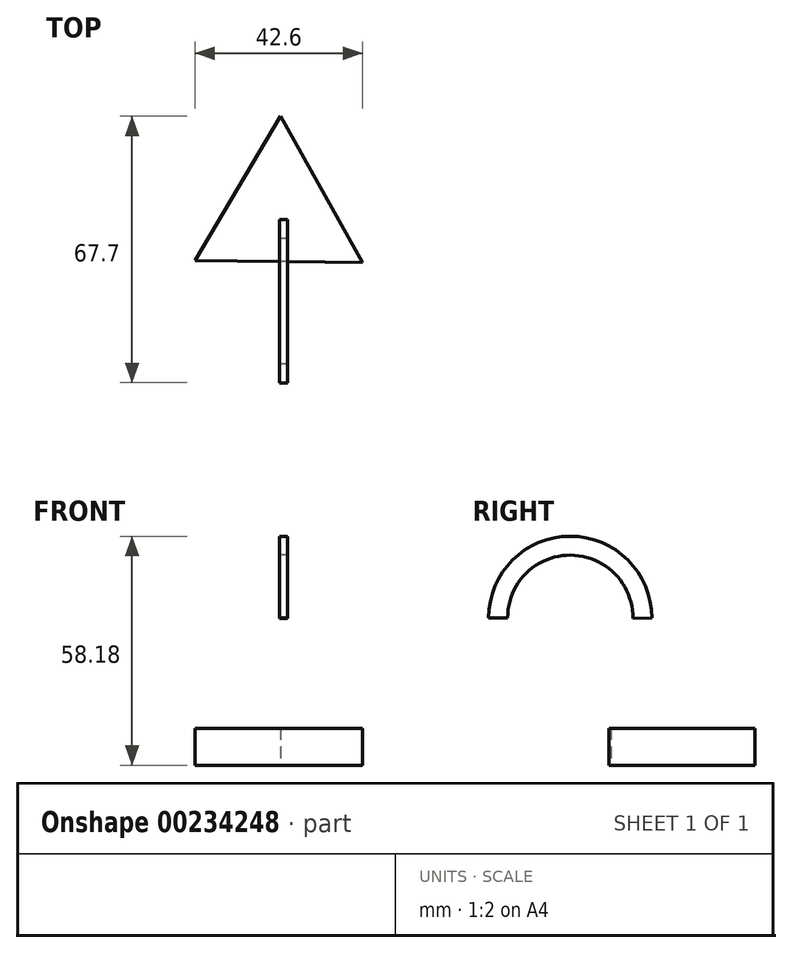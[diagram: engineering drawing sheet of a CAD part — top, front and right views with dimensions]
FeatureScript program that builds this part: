
annotation { "Feature Type Name" : "Feature", "Feature Type Description" : "" }
export const myFeature = defineFeature(function(context is Context, id is Id, definition is map)
    precondition{}
    {
        {
            var Q0;
            Q0=qCreatedBy(makeId("Top.planeOp"),FACE);
            var sketch = newSketch(context, id + "F0", { "sketchPlane" : qUnion([Q0])});
            skCircle(sketch, "E0.cCircle", {"center": v(0, 0) * mm, "radius": 12.3 * mm, "construction": true});
            skLineSegment(sketch, "E0.0", {"start": v(0.32, 24.6) * mm, "end": v(21.14, -12.57) * mm});
            skLineSegment(sketch, "E0.1", {"start": v(21.14, -12.57) * mm, "end": v(-21.46, -12.02) * mm});
            skLineSegment(sketch, "E0.2", {"start": v(-21.46, -12.02) * mm, "end": v(0.32, 24.6) * mm});
            skPoint(sketch, "E0.0.midPoint", {"position": v(10.73, 6.01) * mm});
            skSolve(sketch);
        }
        {
            var Q0;
            Q0=makeQuery(id+"F0.imprint","IMPRINT",FACE,{"disambiguationData":[TD([[makeQuery(id+"F0.imprint","IMPRINT",EDGE,{"derivedFrom":sQuery(id+"F0.wireOp",EDGE,"E0.0")}),-1.0]])]});
            extrude(context, id + "F1", {"entities" : qUnion([Q0]), "depth" : 9.4 * mm});
        }
        {
            var Q0;
            Q0=qCreatedBy(makeId("Right.planeOp"),FACE);
            var sketch = newSketch(context, id + "F2", { "sketchPlane" : qUnion([Q0])});
            skArc(sketch, "E1", {"start": v(-6.47, 37.28) * mm, "mid": v(-22.3, 53.37) * mm, "end": v(-38.3, 37.46) * mm});
            skArc(sketch, "E2", {"start": v(-1.66, 37.46) * mm, "mid": v(-22.38, 58.18) * mm, "end": v(-43.1, 37.46) * mm});
            skLineSegment(sketch, "E3", {"start": v(-43.1, 37.46) * mm, "end": v(-38.3, 37.46) * mm});
            skLineSegment(sketch, "E4", {"start": v(-6.47, 37.28) * mm, "end": v(-1.66, 37.46) * mm});
            skSolve(sketch);
        }
        {
            var Q0;
            Q0 = qSketchRegion(id + "F2", true);
            extrude(context, id + "F3", {"entities" : qUnion([Q0]), "depth" : 2.03 * mm});
        }
    });
